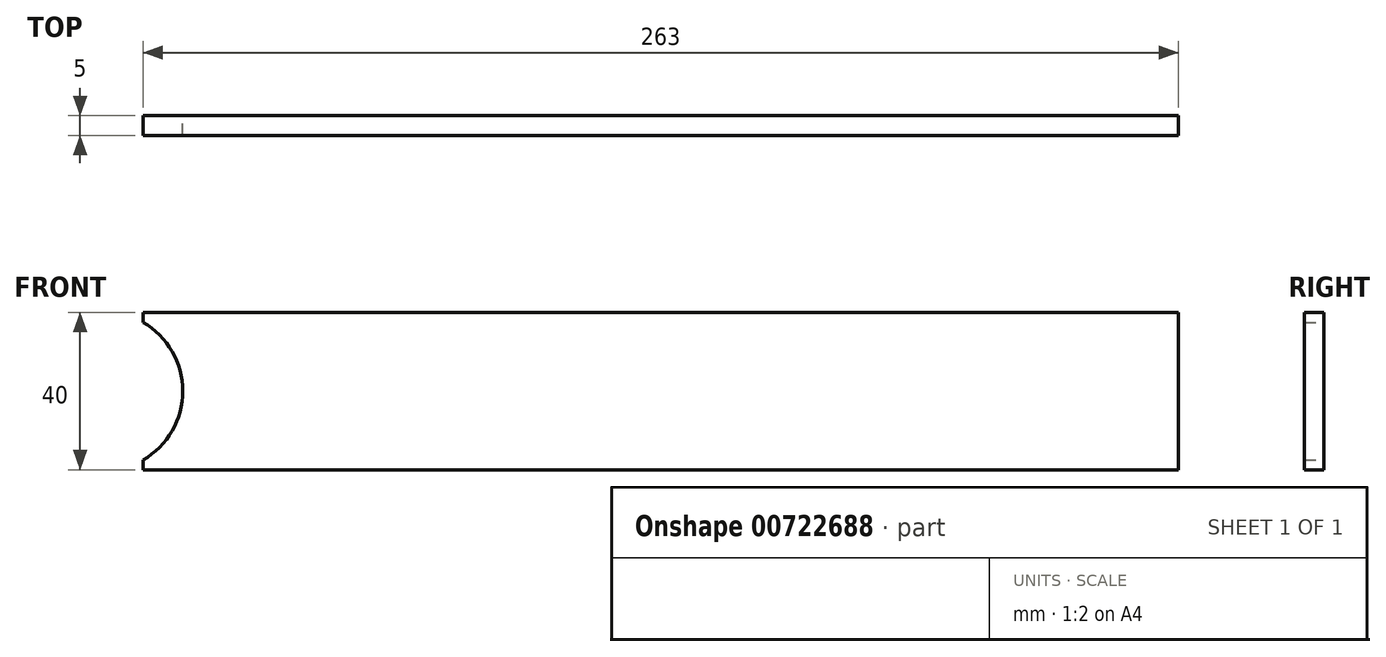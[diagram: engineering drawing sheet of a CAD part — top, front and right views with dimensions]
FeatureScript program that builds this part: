
annotation { "Feature Type Name" : "Feature", "Feature Type Description" : "" }
export const myFeature = defineFeature(function(context is Context, id is Id, definition is map)
    precondition{}
    {
        {
            var Q0;
            Q0=qCreatedBy(makeId("Front.planeOp"),FACE);
            var sketch = newSketch(context, id + "F0", { "sketchPlane" : qUnion([Q0])});
            skLineSegment(sketch, "E0", {"start": v(-57.63, 49.65) * mm, "end": v(205.37, 49.65) * mm});
            skLineSegment(sketch, "E1", {"start": v(205.37, 49.65) * mm, "end": v(205.37, 9.65) * mm});
            skLineSegment(sketch, "E2", {"start": v(205.37, 9.65) * mm, "end": v(-57.63, 9.65) * mm});
            skLineSegment(sketch, "E3", {"start": v(-57.63, 49.65) * mm, "end": v(-57.63, 47.15) * mm});
            skLineSegment(sketch, "E4", {"start": v(-57.63, 9.65) * mm, "end": v(-57.63, 12.15) * mm});
            skLineSegment(sketch, "E5", {"start": v(-47.63, 68.12) * mm, "end": v(-47.63, -14.58) * mm, "construction": true});
            skArc(sketch, "E6", {"start": v(-57.63, 12.15) * mm, "mid": v(-47.6, 29.65) * mm, "end": v(-57.63, 47.15) * mm});
            skSolve(sketch);
        }
        {
            var Q0;
            Q0=makeQuery(id+"F0.imprint","IMPRINT",FACE,{"disambiguationData":[TD([[makeQuery(id+"F0.imprint","IMPRINT",EDGE,{"derivedFrom":sQuery(id+"F0.wireOp",EDGE,"E0")}),-1.0]])]});
            extrude(context, id + "F1", {"entities" : qUnion([Q0]), "depth" : 5 * mm, "offsetDistance" : 25 * mm, "symmetric" : true});
        }
    });
